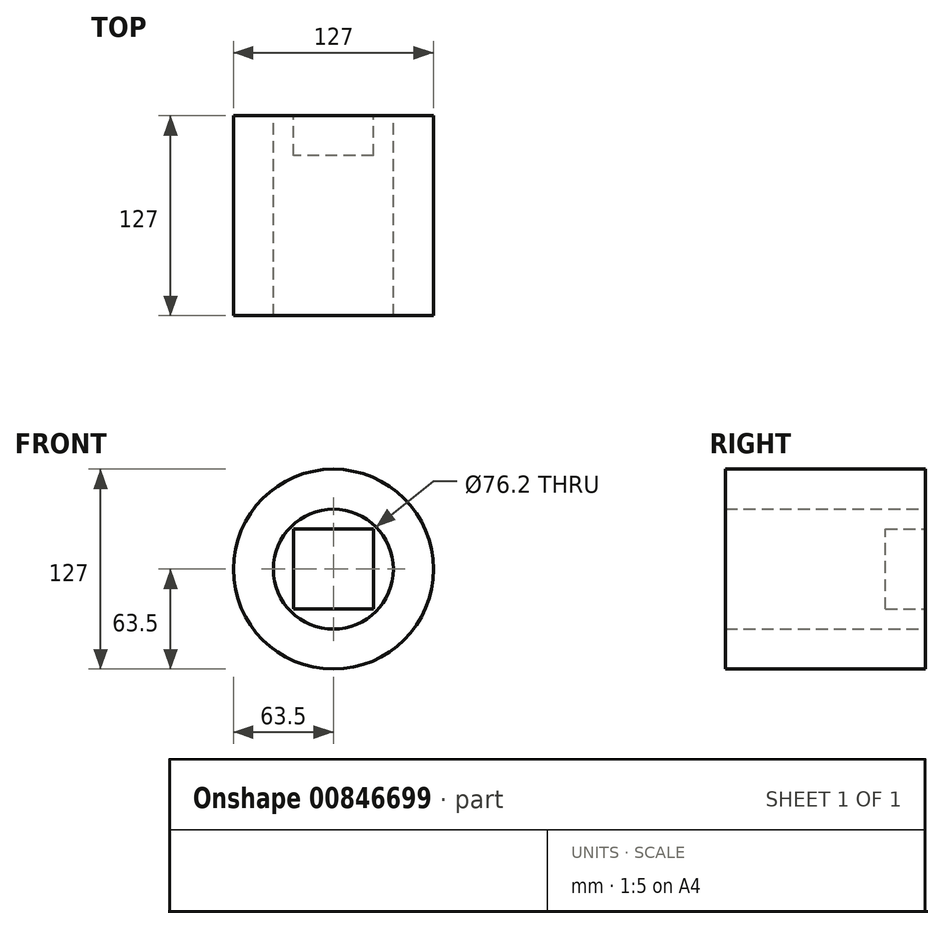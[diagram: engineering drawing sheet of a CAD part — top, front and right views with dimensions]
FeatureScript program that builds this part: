
annotation { "Feature Type Name" : "Feature", "Feature Type Description" : "" }
export const myFeature = defineFeature(function(context is Context, id is Id, definition is map)
    precondition{}
    {
        {
            var Q0;
            Q0=qCreatedBy(makeId("Front.planeOp"),FACE);
            var sketch = newSketch(context, id + "F0", { "sketchPlane" : qUnion([Q0])});
            skCircle(sketch, "E0", {"center": v(0, 0) * mm, "radius": 63.5 * mm});
            skCircle(sketch, "E1", {"center": v(0, 0) * mm, "radius": 50.8 * mm});
            skCircle(sketch, "E2", {"center": v(0, 0) * mm, "radius": 38.1 * mm});
            skPoint(sketch, "E3.center.orphan", {"position": v(0, 50.8) * mm});
            skPoint(sketch, "E4.right.end.orphan", {"position": v(-25.4, 28.4) * mm});
            skPoint(sketch, "E4.left.end.orphan", {"position": v(25.4, 28.4) * mm});
            skPoint(sketch, "E4.bottom.end.orphan", {"position": v(-25.4, -28.4) * mm});
            skPoint(sketch, "E4.bottom.start.orphan", {"position": v(25.4, -28.4) * mm});
            skSolve(sketch);
        }
        {
            var Q0;
            Q0 = qSketchRegion(id + "F0", true);
            var Q1;
            Q1=makeQuery(id+"F0.imprint","IMPRINT",FACE,{"disambiguationData":[TD([[makeQuery(id+"F0.imprint","IMPRINT",EDGE,{"derivedFrom":sQuery(id+"F0.wireOp",EDGE,"E1")}),1.0]])]});
            extrude(context, id + "F1", {"entities" : qUnion([Q0, Q1]), "depth" : 127 * mm, "offsetDistance" : 25.4 * mm});
        }
        {
            var Q0;
            Q0=qCreatedBy(makeId("Front.planeOp"),FACE);
            var sketch = newSketch(context, id + "F2", { "sketchPlane" : qUnion([Q0])});
            skLineSegment(sketch, "E5.bottom", {"start": v(25.4, -25.4) * mm, "end": v(-25.4, -25.4) * mm});
            skLineSegment(sketch, "E5.top", {"start": v(25.4, 25.4) * mm, "end": v(-25.4, 25.4) * mm});
            skLineSegment(sketch, "E5.left", {"start": v(25.4, -25.4) * mm, "end": v(25.4, 25.4) * mm});
            skLineSegment(sketch, "E5.right", {"start": v(-25.4, -25.4) * mm, "end": v(-25.4, 25.4) * mm});
            skPoint(sketch, "E5.middle", {"position": v(0, 0) * mm});
            skSolve(sketch);
        }
        {
            var Q0;
            Q0 = qSketchRegion(id + "F2", true);
            extrude(context, id + "F3", {"entities" : qUnion([Q0]), "depth" : 25.4 * mm, "offsetDistance" : 25.4 * mm});
        }
    });
